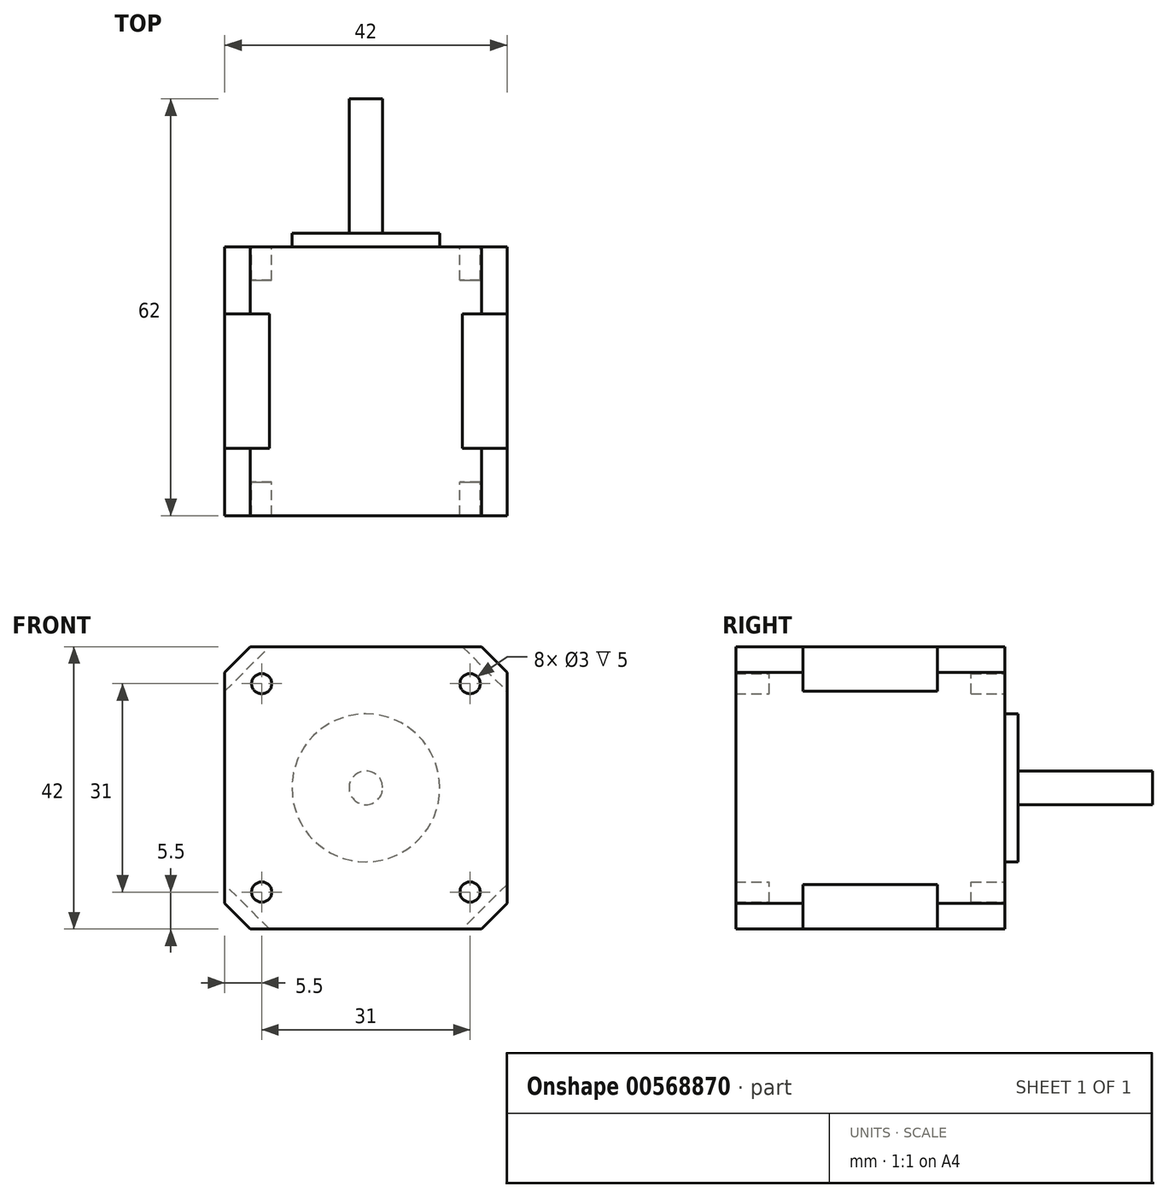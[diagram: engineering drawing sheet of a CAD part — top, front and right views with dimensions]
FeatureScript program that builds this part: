
annotation { "Feature Type Name" : "Feature", "Feature Type Description" : "" }
export const myFeature = defineFeature(function(context is Context, id is Id, definition is map)
    precondition{}
    {
        {
            var Q0;
            Q0=qCreatedBy(makeId("Front.planeOp"),FACE);
            var sketch = newSketch(context, id + "F0", { "sketchPlane" : qUnion([Q0])});
            skLineSegment(sketch, "E0", {"start": v(-21, 17.18) * mm, "end": v(-17.18, 21) * mm});
            skLineSegment(sketch, "E1", {"start": v(-17.18, 21) * mm, "end": v(17.18, 21) * mm});
            skLineSegment(sketch, "E2", {"start": v(17.18, 21) * mm, "end": v(21, 17.18) * mm});
            skLineSegment(sketch, "E3", {"start": v(21, 17.18) * mm, "end": v(21, -17.18) * mm});
            skLineSegment(sketch, "E4", {"start": v(21, -17.18) * mm, "end": v(17.18, -21) * mm});
            skLineSegment(sketch, "E5", {"start": v(17.18, -21) * mm, "end": v(-17.18, -21) * mm});
            skLineSegment(sketch, "E6", {"start": v(-17.18, -21) * mm, "end": v(-21, -17.18) * mm});
            skLineSegment(sketch, "E7", {"start": v(-21, -17.18) * mm, "end": v(-21, 17.18) * mm});
            skLineSegment(sketch, "E8", {"start": v(-21, 14.36) * mm, "end": v(-14.36, 21) * mm});
            skLineSegment(sketch, "E9", {"start": v(14.36, 21) * mm, "end": v(21, 14.36) * mm});
            skLineSegment(sketch, "E10", {"start": v(21, -14.36) * mm, "end": v(14.36, -21) * mm});
            skLineSegment(sketch, "E11", {"start": v(-14.36, -21) * mm, "end": v(-21, -14.36) * mm});
            skCircle(sketch, "E12", {"center": v(0, 0) * mm, "radius": 11 * mm});
            skCircle(sketch, "E13", {"center": v(0, 0) * mm, "radius": 2.5 * mm});
            skLineSegment(sketch, "E14", {"start": v(19.1, 19.1) * mm, "end": v(-19.1, -19.1) * mm, "construction": true});
            skLineSegment(sketch, "E15", {"start": v(19.1, -19.1) * mm, "end": v(-19.1, 19.1) * mm, "construction": true});
            skCircle(sketch, "E16", {"center": v(15.5, 15.5) * mm, "radius": 1.5 * mm});
            skCircle(sketch, "E17", {"center": v(-15.5, 15.5) * mm, "radius": 1.5 * mm});
            skCircle(sketch, "E18", {"center": v(-15.5, -15.5) * mm, "radius": 1.5 * mm});
            skCircle(sketch, "E19", {"center": v(15.5, -15.5) * mm, "radius": 1.5 * mm});
            skLineSegment(sketch, "E20", {"start": v(-21, -17.18) * mm, "end": v(-21, -21) * mm, "construction": true});
            skLineSegment(sketch, "E21", {"start": v(-21, -21) * mm, "end": v(-17.18, -21) * mm, "construction": true});
            skSolve(sketch);
        }
        {
            var Q0;
            {var subQ0=sQuery(id+"F0.wireOp",EDGE,"E8");Q0=makeQuery(id+"F0.imprint","IMPRINT",FACE,{"disambiguationData":[TD([[makeQuery(id+"F0.imprint","IMPRINT",EDGE,{"derivedFrom":subQ0}),-1.0]])]});}
            var Q1;
            Q1=makeQuery(id+"F0.imprint","IMPRINT",FACE,{"disambiguationData":[TD([[makeQuery(id+"F0.imprint","IMPRINT",EDGE,{"derivedFrom":sQuery(id+"F0.wireOp",EDGE,"E12")}),1.0]])]});
            var Q2;
            Q2=makeQuery(id+"F0.imprint","IMPRINT",FACE,{"disambiguationData":[TD([[makeQuery(id+"F0.imprint","IMPRINT",EDGE,{"derivedFrom":sQuery(id+"F0.wireOp",EDGE,"E13")}),1.0]])]});
            extrude(context, id + "F1", {"entities" : qUnion([Q0, Q1, Q2]), "depth" : 40 * mm, "offsetDistance" : 25 * mm});
        }
        {
            var Q0;
            {var subQ0=sQuery(id+"F0.wireOp",EDGE,"E0");Q0=makeQuery(id+"F0.imprint","IMPRINT",FACE,{"disambiguationData":[TD([[makeQuery(id+"F0.imprint","IMPRINT",EDGE,{"derivedFrom":subQ0}),-1.0]])]});}
            var Q1;
            {var subQ0=sQuery(id+"F0.wireOp",EDGE,"E6");Q1=makeQuery(id+"F0.imprint","IMPRINT",FACE,{"disambiguationData":[TD([[makeQuery(id+"F0.imprint","IMPRINT",EDGE,{"derivedFrom":subQ0}),-1.0]])]});}
            var Q2;
            {var subQ0=sQuery(id+"F0.wireOp",EDGE,"E4");Q2=makeQuery(id+"F0.imprint","IMPRINT",FACE,{"disambiguationData":[TD([[makeQuery(id+"F0.imprint","IMPRINT",EDGE,{"derivedFrom":subQ0}),-1.0]])]});}
            var Q3;
            {var subQ0=sQuery(id+"F0.wireOp",EDGE,"E2");Q3=makeQuery(id+"F0.imprint","IMPRINT",FACE,{"disambiguationData":[TD([[makeQuery(id+"F0.imprint","IMPRINT",EDGE,{"derivedFrom":subQ0}),-1.0]])]});}
            var Q4;
            Q4=makeQuery(id+"F1.opExtrude","CAP_FACE",FACE,{"disambiguationData":[OSD([sQuery(id+"F0.wireOp",EDGE,"E1"),sQuery(id+"F0.wireOp",EDGE,"E3"),sQuery(id+"F0.wireOp",EDGE,"E5"),sQuery(id+"F0.wireOp",EDGE,"E7"),sQuery(id+"F0.wireOp",EDGE,"E8"),sQuery(id+"F0.wireOp",EDGE,"E9"),sQuery(id+"F0.wireOp",EDGE,"E10"),sQuery(id+"F0.wireOp",EDGE,"E11")])],"isStart":false});
            var Q5;
            Q5=makeQuery(id+"F1.opExtrude","CAP_FACE",FACE,{"disambiguationData":[OSD([sQuery(id+"F0.wireOp",EDGE,"E1"),sQuery(id+"F0.wireOp",EDGE,"E3"),sQuery(id+"F0.wireOp",EDGE,"E5"),sQuery(id+"F0.wireOp",EDGE,"E7"),sQuery(id+"F0.wireOp",EDGE,"E8"),sQuery(id+"F0.wireOp",EDGE,"E9"),sQuery(id+"F0.wireOp",EDGE,"E10"),sQuery(id+"F0.wireOp",EDGE,"E11")])],"isStart":false});
            extrude(context, id + "F2", {"entities" : qUnion([Q0, Q1, Q2, Q3]), "operationType" : NewBodyOperationType.ADD, "endBound" : BoundingType.UP_TO_SURFACE, "depth" : 25 * mm, "endBoundEntityFace" : qUnion([Q4]), "offsetDistance" : 25 * mm, "hasSecondDirection" : true, "secondDirectionBound" : BoundingType.UP_TO_SURFACE, "secondDirectionOppositeDirection" : false, "secondDirectionDepth" : 25 * mm, "secondDirectionBoundEntityFace" : qUnion([Q5]), "hasSecondDirectionOffset" : true, "secondDirectionOffsetDistance" : 10 * mm});
        }
        {
            var Q0;
            {var subQ0=sQuery(id+"F0.wireOp",EDGE,"E2");Q0=makeQuery(id+"F0.imprint","IMPRINT",FACE,{"disambiguationData":[TD([[makeQuery(id+"F0.imprint","IMPRINT",EDGE,{"derivedFrom":subQ0}),-1.0]])]});}
            var Q1;
            {var subQ0=sQuery(id+"F0.wireOp",EDGE,"E0");Q1=makeQuery(id+"F0.imprint","IMPRINT",FACE,{"disambiguationData":[TD([[makeQuery(id+"F0.imprint","IMPRINT",EDGE,{"derivedFrom":subQ0}),-1.0]])]});}
            var Q2;
            {var subQ0=sQuery(id+"F0.wireOp",EDGE,"E6");Q2=makeQuery(id+"F0.imprint","IMPRINT",FACE,{"disambiguationData":[TD([[makeQuery(id+"F0.imprint","IMPRINT",EDGE,{"derivedFrom":subQ0}),-1.0]])]});}
            var Q3;
            {var subQ0=sQuery(id+"F0.wireOp",EDGE,"E4");Q3=makeQuery(id+"F0.imprint","IMPRINT",FACE,{"disambiguationData":[TD([[makeQuery(id+"F0.imprint","IMPRINT",EDGE,{"derivedFrom":subQ0}),-1.0]])]});}
            extrude(context, id + "F3", {"entities" : qUnion([Q0, Q1, Q2, Q3]), "operationType" : NewBodyOperationType.ADD, "depth" : 10 * mm, "offsetDistance" : 25 * mm});
        }
        {
            var Q0;
            Q0=makeQuery(id+"F0.imprint","IMPRINT",FACE,{"disambiguationData":[TD([[makeQuery(id+"F0.imprint","IMPRINT",EDGE,{"derivedFrom":sQuery(id+"F0.wireOp",EDGE,"E12")}),1.0]])]});
            extrude(context, id + "F4", {"entities" : qUnion([Q0]), "operationType" : NewBodyOperationType.ADD, "oppositeDirection" : true, "depth" : 2 * mm, "offsetDistance" : 25 * mm});
        }
        {
            var Q0;
            Q0=makeQuery(id+"F0.imprint","IMPRINT",FACE,{"disambiguationData":[TD([[makeQuery(id+"F0.imprint","IMPRINT",EDGE,{"derivedFrom":sQuery(id+"F0.wireOp",EDGE,"E13")}),1.0]])]});
            extrude(context, id + "F5", {"entities" : qUnion([Q0]), "operationType" : NewBodyOperationType.ADD, "oppositeDirection" : true, "depth" : 22 * mm, "offsetDistance" : 25 * mm});
        }
        {
            var Q0;
            Q0=makeQuery(id+"F0.imprint","IMPRINT",FACE,{"disambiguationData":[TD([[makeQuery(id+"F0.imprint","IMPRINT",EDGE,{"derivedFrom":sQuery(id+"F0.wireOp",EDGE,"E16")}),1.0]])]});
            var Q1;
            Q1=makeQuery(id+"F0.imprint","IMPRINT",FACE,{"disambiguationData":[TD([[makeQuery(id+"F0.imprint","IMPRINT",EDGE,{"derivedFrom":sQuery(id+"F0.wireOp",EDGE,"E17")}),1.0]])]});
            var Q2;
            Q2=makeQuery(id+"F0.imprint","IMPRINT",FACE,{"disambiguationData":[TD([[makeQuery(id+"F0.imprint","IMPRINT",EDGE,{"derivedFrom":sQuery(id+"F0.wireOp",EDGE,"E18")}),1.0]])]});
            var Q3;
            Q3=makeQuery(id+"F0.imprint","IMPRINT",FACE,{"disambiguationData":[TD([[makeQuery(id+"F0.imprint","IMPRINT",EDGE,{"derivedFrom":sQuery(id+"F0.wireOp",EDGE,"E19")}),1.0]])]});
            var Q4;
            {var subQ0=sQuery(id+"F0.wireOp",EDGE,"E19");var subQ1=sQuery(id+"F0.wireOp",EDGE,"E18");var subQ2=sQuery(id+"F0.wireOp",EDGE,"E17");var subQ3=sQuery(id+"F0.wireOp",EDGE,"E16");var subQ4=sQuery(id+"F0.wireOp",EDGE,"E11");var subQ5=sQuery(id+"F0.wireOp",EDGE,"E10");var subQ6=sQuery(id+"F0.wireOp",EDGE,"E9");var subQ7=sQuery(id+"F0.wireOp",EDGE,"E8");var subQ8=sQuery(id+"F0.wireOp",EDGE,"E7");var subQ9=sQuery(id+"F0.wireOp",EDGE,"E5");var subQ10=sQuery(id+"F0.wireOp",EDGE,"E3");var subQ11=sQuery(id+"F0.wireOp",EDGE,"E1");Q4=makeQuery(id+"F2.boolean.opBoolean","MERGE",FACE,{"derivedFrom":[makeQuery(id+"F1.opExtrude","CAP_FACE",FACE,{"disambiguationData":[OSD([subQ11,subQ10,subQ9,subQ8,subQ7,subQ6,subQ5,subQ4,subQ3,subQ2,subQ1,subQ0])],"isStart":false}),makeQuery(id+"F2.opExtrude","CAP_FACE",FACE,{"disambiguationData":[OSD([subQ11,subQ10,subQ9,subQ8,subQ7,subQ6,subQ5,subQ4,subQ3,subQ2,subQ1,subQ0]),OD(0.0)],"isStart":false}),makeQuery(id+"F2.opExtrude","CAP_FACE",FACE,{"disambiguationData":[OSD([subQ11,subQ10,subQ9,subQ8,subQ7,subQ6,subQ5,subQ4,subQ3,subQ2,subQ1,subQ0]),OD(1.0)],"isStart":false}),makeQuery(id+"F2.opExtrude","CAP_FACE",FACE,{"disambiguationData":[OSD([subQ11,subQ10,subQ9,subQ8,subQ7,subQ6,subQ5,subQ4,subQ3,subQ2,subQ1,subQ0]),OD(2.0)],"isStart":false}),makeQuery(id+"F2.opExtrude","CAP_FACE",FACE,{"disambiguationData":[OSD([subQ11,subQ10,subQ9,subQ8,subQ7,subQ6,subQ5,subQ4,subQ3,subQ2,subQ1,subQ0]),OD(3.0)],"isStart":false})]});}
            extrude(context, id + "F6", {"entities" : qUnion([Q0, Q1, Q2, Q3]), "operationType" : NewBodyOperationType.ADD, "endBound" : BoundingType.UP_TO_SURFACE, "depth" : 25 * mm, "endBoundEntityFace" : qUnion([Q4]), "hasOffset" : true, "offsetDistance" : 5 * mm, "hasSecondDirection" : true, "secondDirectionOppositeDirection" : false, "secondDirectionDepth" : 5 * mm});
        }
    });
